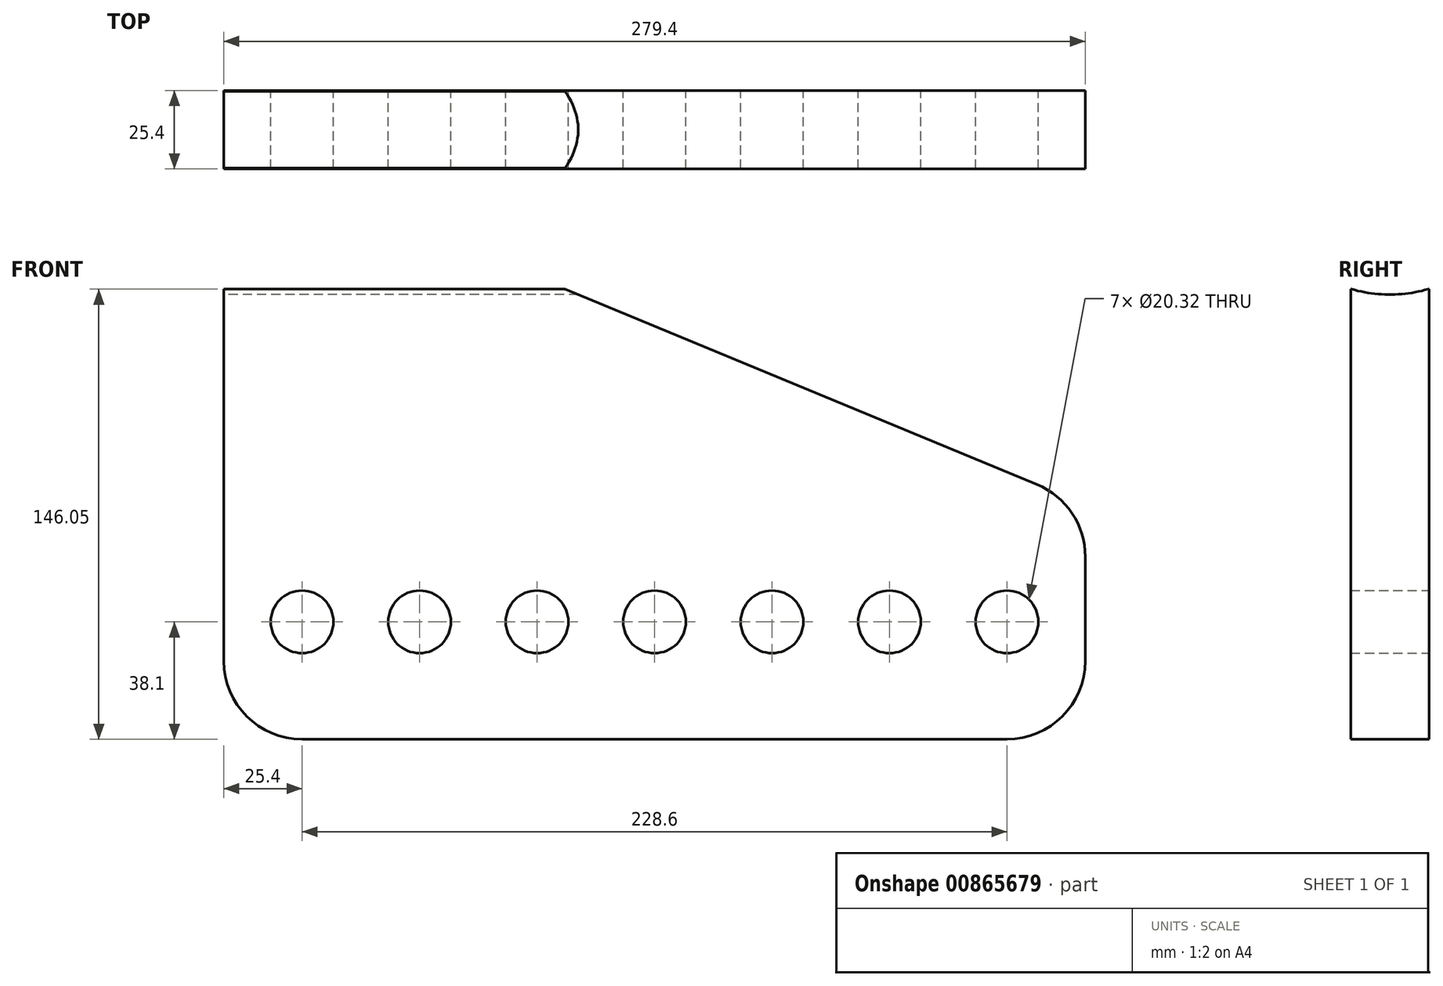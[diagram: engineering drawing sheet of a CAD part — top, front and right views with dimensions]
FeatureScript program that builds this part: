
annotation { "Feature Type Name" : "Feature", "Feature Type Description" : "" }
export const myFeature = defineFeature(function(context is Context, id is Id, definition is map)
    precondition{}
    {
        {
            var Q0;
            Q0=qCreatedBy(makeId("Front.planeOp"),FACE);
            var sketch = newSketch(context, id + "F0", { "sketchPlane" : qUnion([Q0])});
            skCircle(sketch, "E0", {"center": v(25.4, 38.1) * mm, "radius": 10.16 * mm});
            skCircle(sketch, "E1.1.0.0", {"center": v(63.5, 38.1) * mm, "radius": 10.16 * mm});
            skCircle(sketch, "E1.2.0.0", {"center": v(101.6, 38.1) * mm, "radius": 10.16 * mm});
            skCircle(sketch, "E1.3.0.0", {"center": v(139.7, 38.1) * mm, "radius": 10.16 * mm});
            skCircle(sketch, "E1.4.0.0", {"center": v(177.8, 38.1) * mm, "radius": 10.16 * mm});
            skCircle(sketch, "E1.5.0.0", {"center": v(215.9, 38.1) * mm, "radius": 10.16 * mm});
            skCircle(sketch, "E1.6.0.0", {"center": v(254, 38.1) * mm, "radius": 10.16 * mm});
            skLineSegment(sketch, "E1.direction1", {"start": v(25.4, 38.1) * mm, "end": v(63.5, 38.1) * mm, "construction": true});
            skLineSegment(sketch, "E2", {"start": v(25.4, 0) * mm, "end": v(221.63, 0) * mm, "construction": true});
            skLineSegment(sketch, "E3", {"start": v(0, 25.4) * mm, "end": v(0, 146.05) * mm});
            skLineSegment(sketch, "E4", {"start": v(0, 146.05) * mm, "end": v(110.68, 146.05) * mm});
            skLineSegment(sketch, "E5", {"start": v(110.68, 146.05) * mm, "end": v(263.72, 82.7) * mm});
            skLineSegment(sketch, "E6", {"start": v(279.4, 59.22) * mm, "end": v(279.4, 25.4) * mm});
            skLineSegment(sketch, "E7", {"start": v(254, 0) * mm, "end": v(0, 0) * mm});
            skPoint(sketch, "E8.visualSharp", {"position": v(279.4, 76.2) * mm});
            skArc(sketch, "E8.filletArc", {"start": v(279.4, 59.22) * mm, "mid": v(275.12, 73.34) * mm, "end": v(263.72, 82.7) * mm});
            skPoint(sketch, "E9.visualSharp", {"position": v(279.4, 0) * mm});
            skArc(sketch, "E9.filletArc", {"start": v(254, 0) * mm, "mid": v(271.96, 7.44) * mm, "end": v(279.4, 25.4) * mm});
            skPoint(sketch, "E10.visualSharp", {"position": v(0, 0) * mm});
            skArc(sketch, "E10.filletArc", {"start": v(0, 25.4) * mm, "mid": v(7.44, 7.44) * mm, "end": v(25.4, 0) * mm});
            skSolve(sketch);
        }
        {
            var Q0;
            Q0=makeQuery(id+"F0.imprint","IMPRINT",FACE,{"disambiguationData":[TD([[makeQuery(id+"F0.imprint","IMPRINT",EDGE,{"derivedFrom":sQuery(id+"F0.wireOp",EDGE,"E0")}),-1.0]])]});
            extrude(context, id + "F1", {"entities" : qUnion([Q0]), "depth" : 25.4 * mm, "offsetDistance" : 25.4 * mm});
        }
        {
            var Q0;
            Q0=makeQuery(id+"F1.opExtrude","SWEPT_FACE",FACE,{"disambiguationData":[OSD([sQuery(id+"F0.wireOp",EDGE,"E3")])]});
            var sketch = newSketch(context, id + "F2", { "sketchPlane" : qUnion([Q0])});
            skCircle(sketch, "E11", {"center": v(12.7, 188.72) * mm, "radius": 44.45 * mm});
            skPoint(sketch, "E11.centerSnap0", {"position": v(12.7, 146.05) * mm});
            skSolve(sketch);
        }
        {
            var Q0;
            {var subQ0=sQuery(id+"F2.wireOp",EDGE,"E11");var subQ1=makeQuery(id+"F1.opExtrude","SWEPT_EDGE",EDGE,{"disambiguationData":[OSD([sQuery(id+"F0.wireOp",EDGE,"E3"),sQuery(id+"F0.wireOp",EDGE,"E4")])]});var subQ2=makeQuery(id+"F2.imprint","INTERSECT",VERTEX,{"disambiguationData":[OD(0.0)],"derivedFrom":[subQ1,subQ0]});Q0=makeQuery(id+"F2.imprint","IMPRINT",FACE,{"disambiguationData":[TD([[makeQuery(id+"F2.imprint","IMPRINT",EDGE,{"disambiguationData":[TD([[subQ2,-1.0]])],"derivedFrom":subQ0}),1.0]])]});}
            extrude(context, id + "F3", {"entities" : qUnion([Q0]), "operationType" : NewBodyOperationType.REMOVE, "oppositeDirection" : true, "depth" : 152.4 * mm, "offsetDistance" : 25.4 * mm});
        }
    });
